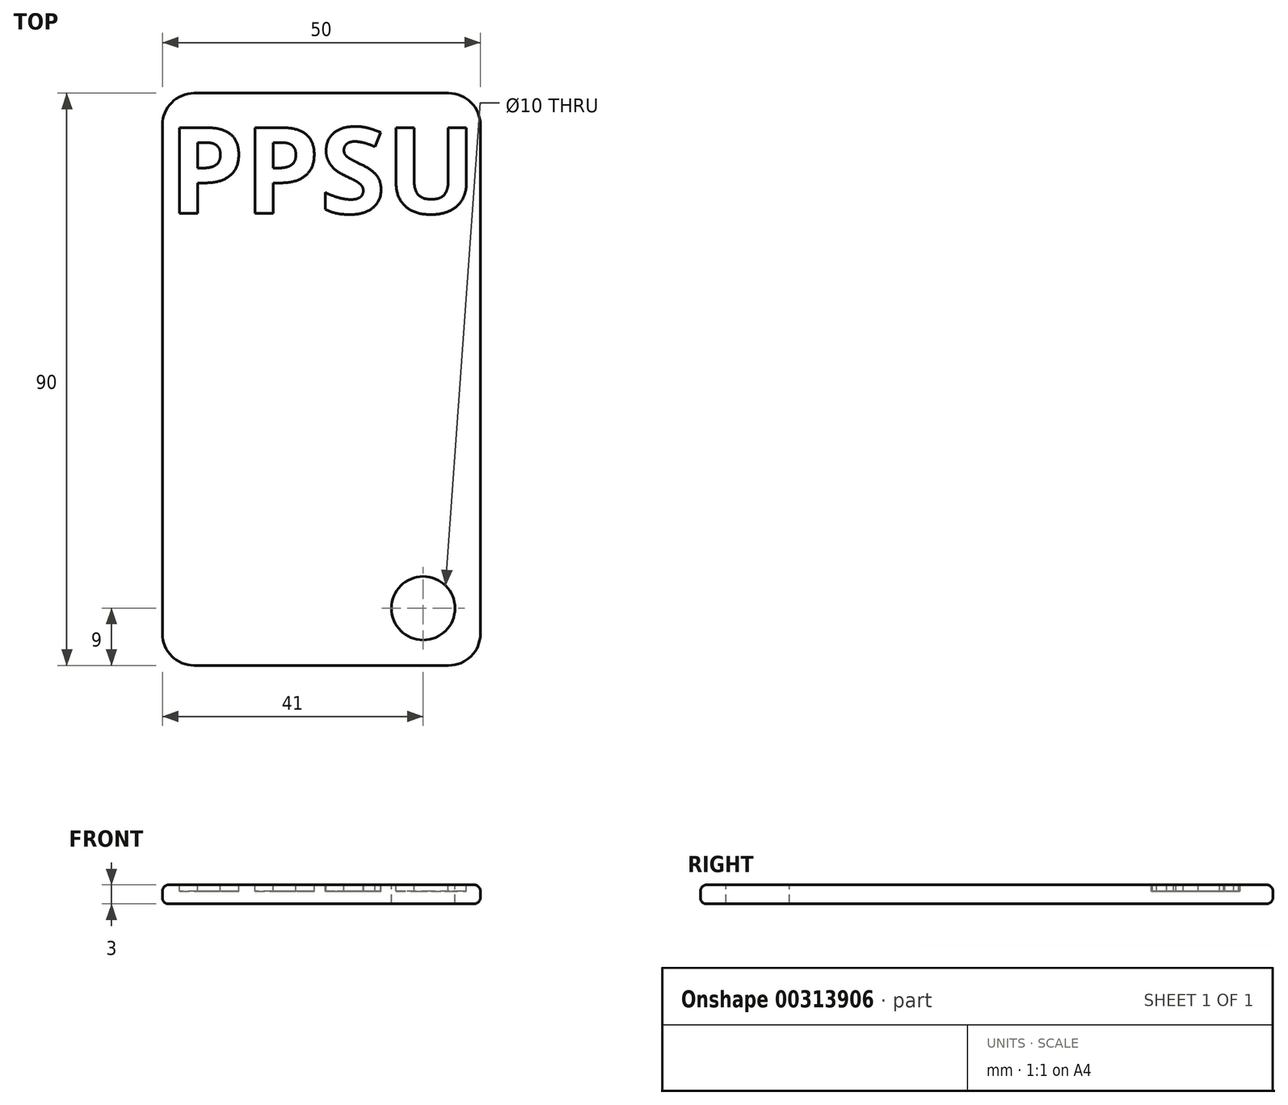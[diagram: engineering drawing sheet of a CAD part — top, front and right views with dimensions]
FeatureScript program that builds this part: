
annotation { "Feature Type Name" : "Feature", "Feature Type Description" : "" }
export const myFeature = defineFeature(function(context is Context, id is Id, definition is map)
    precondition{}
    {
        {
            var Q0;
            Q0=qCreatedBy(makeId("Top.planeOp"),FACE);
            var sketch = newSketch(context, id + "F0", { "sketchPlane" : qUnion([Q0])});
            skLineSegment(sketch, "E0.bottom", {"start": v(-45, 25) * mm, "end": v(45, 25) * mm});
            skLineSegment(sketch, "E0.top", {"start": v(-45, -25) * mm, "end": v(45, -25) * mm});
            skLineSegment(sketch, "E0.left", {"start": v(-45, 25) * mm, "end": v(-45, -25) * mm});
            skLineSegment(sketch, "E0.right", {"start": v(45, 25) * mm, "end": v(45, -25) * mm});
            skLineSegment(sketch, "E1", {"start": v(-45, 25) * mm, "end": v(45, -25) * mm, "construction": true});
            skSolve(sketch);
        }
        {
            var Q0;
            Q0=makeQuery(id+"F0.imprint","IMPRINT",FACE,{"disambiguationData":[TD([[makeQuery(id+"F0.imprint","IMPRINT",EDGE,{"derivedFrom":sQuery(id+"F0.wireOp",EDGE,"E0.bottom")}),-1.0]])]});
            extrude(context, id + "F1", {"entities" : qUnion([Q0]), "depth" : 3 * mm});
        }
        {
            var Q0;
            Q0=makeQuery(id+"F1.opExtrude","CAP_FACE",FACE,{"disambiguationData":[OSD([sQuery(id+"F0.wireOp",EDGE,"E0.bottom"),sQuery(id+"F0.wireOp",EDGE,"E0.top"),sQuery(id+"F0.wireOp",EDGE,"E0.left"),sQuery(id+"F0.wireOp",EDGE,"E0.right")])],"isStart":false});
            var Q1;
            Q1=makeQuery(id+"F1.opExtrude","CAP_FACE",FACE,{"disambiguationData":[OSD([sQuery(id+"F0.wireOp",EDGE,"E0.bottom"),sQuery(id+"F0.wireOp",EDGE,"E0.top"),sQuery(id+"F0.wireOp",EDGE,"E0.left"),sQuery(id+"F0.wireOp",EDGE,"E0.right")])],"isStart":true});
            fillet(context, id + "F2", {"entities" : qUnion([Q0, Q1]), "radius" : 1 * mm, "tangentPropagation" : true, "allowEdgeOverflow" : false});
        }
        {
            var Q0;
            Q0=makeQuery(id+"F1.opExtrude","SWEPT_EDGE",EDGE,{"disambiguationData":[OSD([sQuery(id+"F0.wireOp",EDGE,"E0.top"),sQuery(id+"F0.wireOp",EDGE,"E0.right")])]});
            var Q1;
            Q1=makeQuery(id+"F1.opExtrude","SWEPT_EDGE",EDGE,{"disambiguationData":[OSD([sQuery(id+"F0.wireOp",EDGE,"E0.bottom"),sQuery(id+"F0.wireOp",EDGE,"E0.right")])]});
            var Q2;
            Q2=makeQuery(id+"F1.opExtrude","SWEPT_EDGE",EDGE,{"disambiguationData":[OSD([sQuery(id+"F0.wireOp",EDGE,"E0.bottom"),sQuery(id+"F0.wireOp",EDGE,"E0.left")])]});
            var Q3;
            Q3=makeQuery(id+"F1.opExtrude","SWEPT_EDGE",EDGE,{"disambiguationData":[OSD([sQuery(id+"F0.wireOp",EDGE,"E0.top"),sQuery(id+"F0.wireOp",EDGE,"E0.left")])]});
            fillet(context, id + "F3", {"entities" : qUnion([Q0, Q1, Q2, Q3]), "radius" : 5 * mm, "tangentPropagation" : true, "allowEdgeOverflow" : false});
        }
        {
            var Q0;
            Q0=qCreatedBy(makeId("Right.planeOp"),FACE);
            var sketch = newSketch(context, id + "F4", { "sketchPlane" : qUnion([Q0])});
            skLineSegment(sketch, "E2", {"start": v(0, 0) * mm, "end": v(0, 32.9) * mm});
            skSolve(sketch);
        }
        {
            var Q0;
            Q0=makeQuery(id+"F1.opExtrude","SWEPT_BODY",BODY,{"disambiguationData":[OSD([sQuery(id+"F0.wireOp",EDGE,"E0.bottom"),sQuery(id+"F0.wireOp",EDGE,"E0.top"),sQuery(id+"F0.wireOp",EDGE,"E0.left"),sQuery(id+"F0.wireOp",EDGE,"E0.right")])]});
            var Q1;
            Q1=sQuery(id+"F4.wireOp",EDGE,"E2");
            transform(context, id + "F5", {"entities" : qUnion([Q0]), "transformType" : TransformType.ROTATION, "transformAxis" : qUnion([Q1]), "angle" : 90 * degree, "makeCopy" : false});
        }
        {
            var Q0;
            Q0=makeQuery(id+"F1.opExtrude","CAP_FACE",FACE,{"disambiguationData":[OSD([sQuery(id+"F0.wireOp",EDGE,"E0.bottom"),sQuery(id+"F0.wireOp",EDGE,"E0.top"),sQuery(id+"F0.wireOp",EDGE,"E0.left"),sQuery(id+"F0.wireOp",EDGE,"E0.right")])],"isStart":false});
            var sketch = newSketch(context, id + "F6", { "sketchPlane" : qUnion([Q0])});
            skText(sketch, "E3", { "text": "PPSU", "fontName": "OpenSans-Bold.ttf"});
            const initialGuessF6  = {"E3": [-0.024, 0.0261, 1, 0, 0.0136]};
            skSetInitialGuess(sketch, initialGuessF6);
            skSolve(sketch);
        }
        {
            var Q0;
            Q0=qSketchRegion(id+"F6",true);
            extrude(context, id + "F7", {"entities" : qUnion([Q0]), "operationType" : NewBodyOperationType.REMOVE, "oppositeDirection" : true, "depth" : 1 * mm});
        }
        {
            var Q0;
            {var subQ0=sQuery(id+"F0.wireOp",EDGE,"E0.left");var subQ2=sQuery(id+"F0.wireOp",EDGE,"E0.bottom");var subQ4=sQuery(id+"F0.wireOp",EDGE,"E0.right");var subQ6=sQuery(id+"F0.wireOp",EDGE,"E0.top");Q0=makeQuery(id+"F7.boolean.opBoolean","SPLIT",FACE,{"disambiguationData":[TD([makeQuery(id+"F7.opExtrude","SWEPT_FACE",FACE,{"disambiguationData":[OSD([sQuery(id+"F6.wireOp",EDGE,"E3.sketch_text.stroke-0")])]})])],"derivedFrom":makeQuery(id+"F1.opExtrude","CAP_FACE",FACE,{"disambiguationData":[OSD([subQ2,subQ6,subQ0,subQ4])],"isStart":false})});}
            var sketch = newSketch(context, id + "F8", { "sketchPlane" : qUnion([Q0])});
            skCircle(sketch, "E4", {"center": v(16, -36) * mm, "radius": 5 * mm});
            skSolve(sketch);
        }
        {
            var Q0;
            Q0=qSketchRegion(id+"F8",true);
            extrude(context, id + "F9", {"entities" : qUnion([Q0]), "operationType" : NewBodyOperationType.REMOVE, "oppositeDirection" : true, "depth" : 3 * mm});
        }
    });
